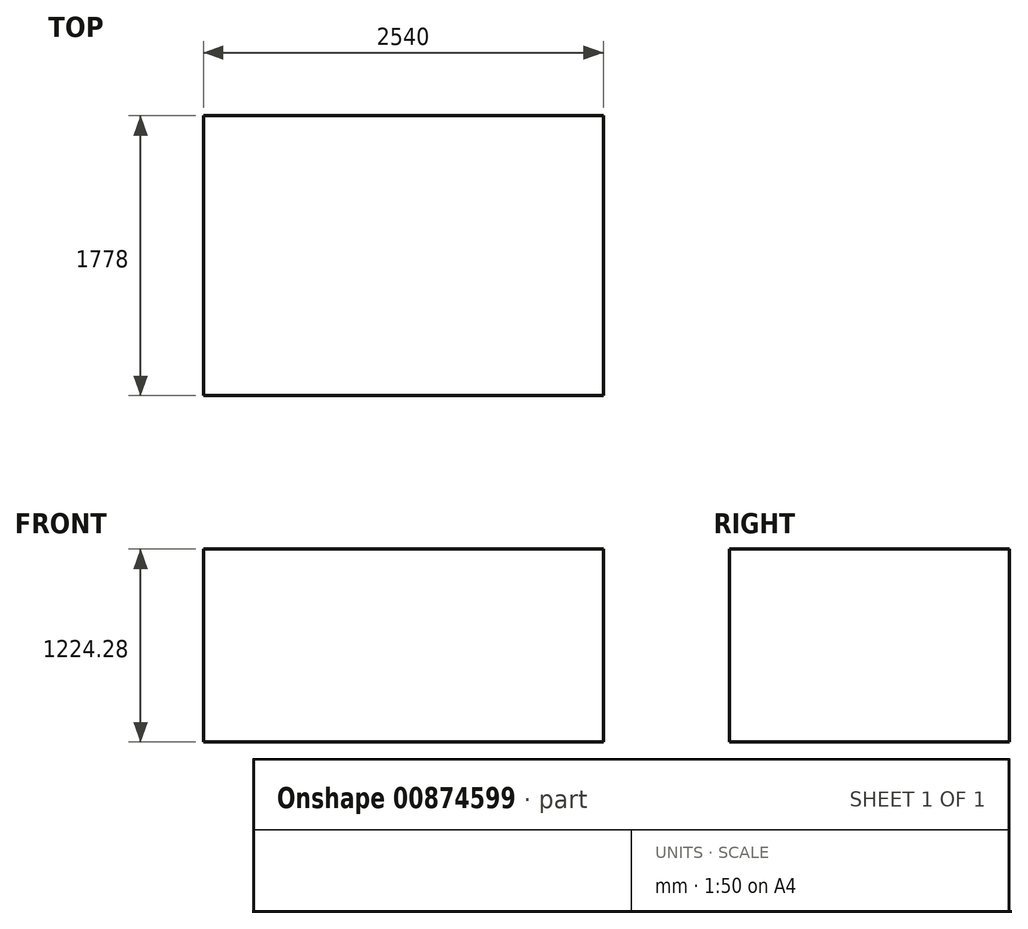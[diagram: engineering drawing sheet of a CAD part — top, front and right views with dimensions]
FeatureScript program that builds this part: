
annotation { "Feature Type Name" : "Feature", "Feature Type Description" : "" }
export const myFeature = defineFeature(function(context is Context, id is Id, definition is map)
    precondition{}
    {
        {
            var Q0;
            Q0=qCreatedBy(makeId("Top.planeOp"),FACE);
            var sketch = newSketch(context, id + "F0", { "sketchPlane" : qUnion([Q0])});
            skLineSegment(sketch, "E0.bottom", {"start": v(2426.77, 1712.8) * mm, "end": v(-113.23, 1712.8) * mm});
            skLineSegment(sketch, "E0.top", {"start": v(2426.77, -65.2) * mm, "end": v(-113.23, -65.2) * mm});
            skLineSegment(sketch, "E0.left", {"start": v(2426.77, 1712.8) * mm, "end": v(2426.77, -65.2) * mm});
            skLineSegment(sketch, "E0.right", {"start": v(-113.23, 1712.8) * mm, "end": v(-113.23, -65.2) * mm});
            skSolve(sketch);
        }
        {
            var Q0;
            Q0=makeQuery(id+"F0.imprint","IMPRINT",FACE,{"disambiguationData":[TD([[makeQuery(id+"F0.imprint","IMPRINT",EDGE,{"derivedFrom":sQuery(id+"F0.wireOp",EDGE,"E0.bottom")}),1.0]])]});
            extrude(context, id + "F1", {"entities" : qUnion([Q0]), "depth" : 1224.28 * mm, "offsetDistance" : 25.4 * mm});
        }
    });
